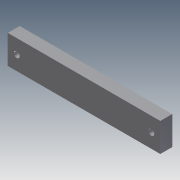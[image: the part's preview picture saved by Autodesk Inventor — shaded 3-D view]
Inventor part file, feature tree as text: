
AUTODESK INVENTOR PART (.ipt)
format: ipt  version: 2011 (Build 150239000, 239)  size: 78,848 bytes
history: native  units: in
note: dims shown in document units (in); Inventor stores cm internally (conversion verified against a paired STEP export)
features: extrude x2, sketch x2
ambient origin geometry x8: Origin, YZ Plane, XZ Plane, XY Plane, X Axis, Y Axis, Z Axis, Center Point
bodies: Solid1 (feature_tree)
feature tree (4):
  extrude  "Extrusion1"  Depth=0.75in
  extrude  "Extrusion2"  Depth=1.765in
  sketch  "Sketch1"  dims[d0=4.0in d1=0.75in]
  sketch  "Sketch2"  dims[d2=0.3125in d3=0.0in d4=1.765in d5=3.53in d6=0.156in d7=0.3125in d8=0.0in]
